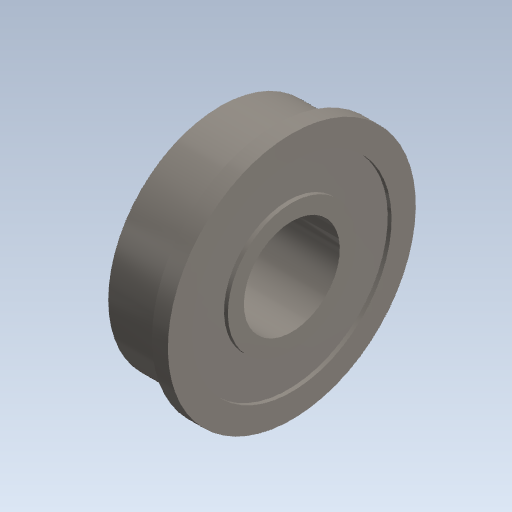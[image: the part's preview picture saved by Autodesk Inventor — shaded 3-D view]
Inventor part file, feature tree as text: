
AUTODESK INVENTOR PART (.ipt)
format: ipt  version: 2020 (Build 240168000, 168)  size: 110,592 bytes
history: native  units: mm (DEFAULTED — no unit token found)
features: revolve x1
ambient origin geometry x8: Origin, YZ Plane, XZ Plane, XY Plane, X Axis, Y Axis, Z Axis, Center Point
bodies: Solid1 (feature_tree)
feature tree (1):
  revolve  "Revolve1"  [1 undecoded]
note: 1 required parameter value undecoded (feature->parameter linkage not recoverable at this tier; creation-order binding heuristic only, values carry confidence <= 0.55)
